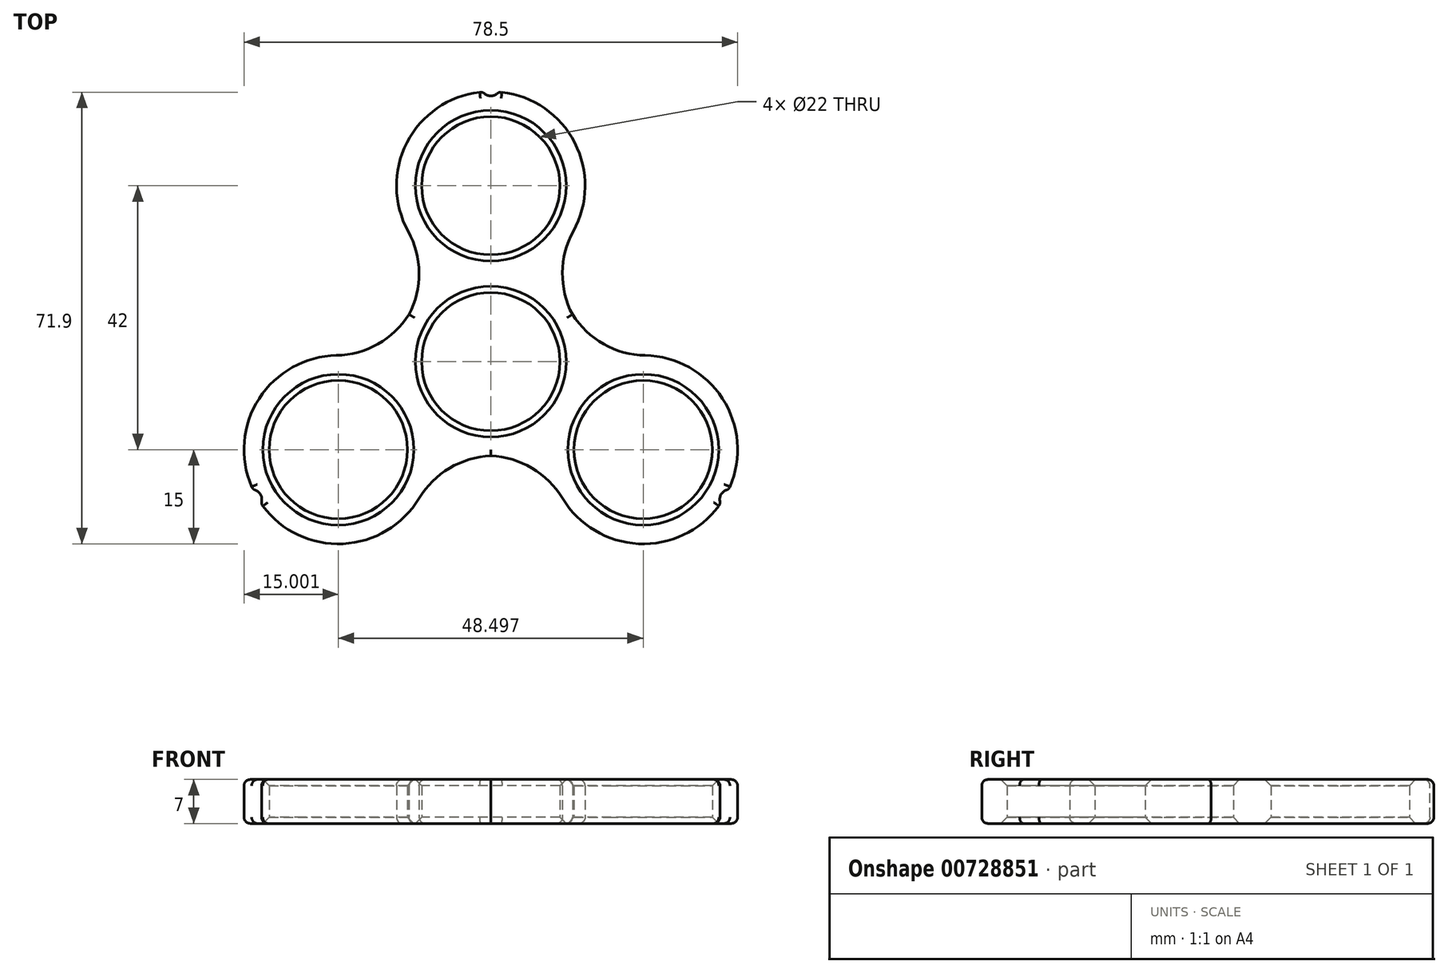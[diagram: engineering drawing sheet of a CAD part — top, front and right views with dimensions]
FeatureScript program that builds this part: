
annotation { "Feature Type Name" : "Feature", "Feature Type Description" : "" }
export const myFeature = defineFeature(function(context is Context, id is Id, definition is map)
    precondition{}
    {
        {
            var Q0;
            Q0=qCreatedBy(makeId("Top.planeOp"),FACE);
            var sketch = newSketch(context, id + "F0", { "sketchPlane" : qUnion([Q0])});
            skCircle(sketch, "E0", {"center": v(0, 0) * mm, "radius": 11 * mm});
            skCircle(sketch, "E1", {"center": v(0, 28) * mm, "radius": 11 * mm});
            skArc(sketch, "E2", {"start": v(12.67, 19.96) * mm, "mid": v(0, 43) * mm, "end": v(-12.67, 19.96) * mm});
            skArc(sketch, "E3", {"start": v(-12.67, 8.04) * mm, "mid": v(0, -15) * mm, "end": v(12.67, 8.04) * mm});
            skArc(sketch, "E4", {"start": v(13.14, 20.76) * mm, "mid": v(11.4, 14) * mm, "end": v(13.14, 7.24) * mm});
            skArc(sketch, "E5", {"start": v(-13.14, 7.24) * mm, "mid": v(-11.4, 14) * mm, "end": v(-13.14, 20.76) * mm});
            skSolve(sketch);
        }
        {
            var Q0;
            Q0=makeQuery(id+"F0.imprint","IMPRINT",FACE,{"disambiguationData":[TD([[makeQuery(id+"F0.imprint","IMPRINT",EDGE,{"derivedFrom":sQuery(id+"F0.wireOp",EDGE,"E0")}),-1.0]])]});
            extrude(context, id + "F1", {"entities" : qUnion([Q0]), "depth" : 7 * mm, "offsetDistance" : 25 * mm});
        }
        {
            var Q0;
            Q0=makeQuery(id+"F1.opExtrude","CAP_EDGE",EDGE,{"disambiguationData":[OSD([sQuery(id+"F0.wireOp",EDGE,"E2")])],"isStart":false});
            var Q1;
            Q1=makeQuery(id+"F1.opExtrude","CAP_EDGE",EDGE,{"disambiguationData":[OSD([sQuery(id+"F0.wireOp",EDGE,"E2")])],"isStart":true});
            fillet(context, id + "F2", {"entities" : qUnion([Q0, Q1]), "radius" : 1 * mm, "tangentPropagation" : true, "allowEdgeOverflow" : false});
        }
        {
            var Q0;
            Q0=qCreatedBy(makeId("Top.planeOp"),FACE);
            var sketch = newSketch(context, id + "F3", { "sketchPlane" : qUnion([Q0])});
            skCircle(sketch, "E6", {"center": v(0, 43.78) * mm, "radius": 1.5 * mm});
            skSolve(sketch);
        }
        {
            var Q0;
            Q0=makeQuery(id+"F3.imprint","IMPRINT",FACE,{"disambiguationData":[TD([[makeQuery(id+"F3.imprint","IMPRINT",EDGE,{"derivedFrom":sQuery(id+"F3.wireOp",EDGE,"E6")}),1.0]])]});
            extrude(context, id + "F4", {"entities" : qUnion([Q0]), "operationType" : NewBodyOperationType.REMOVE, "oppositeDirection" : true, "depth" : 25 * mm, "offsetDistance" : 25 * mm, "hasSecondDirection" : true, "secondDirectionOppositeDirection" : false, "secondDirectionDepth" : 25 * mm});
        }
        {
            var Q0;
            Q0=makeQuery(id+"F4.boolean.opBoolean","INTERSECT",EDGE,{"disambiguationData":[OD(1.0)],"derivedFrom":[makeQuery(id+"F1.opExtrude","SWEPT_FACE",FACE,{"disambiguationData":[OSD([sQuery(id+"F0.wireOp",EDGE,"E2")])]}),makeQuery(id+"F4.opExtrude","SWEPT_FACE",FACE,{"disambiguationData":[OSD([sQuery(id+"F3.wireOp",EDGE,"E6")])]})]});
            fillet(context, id + "F5", {"entities" : qUnion([Q0]), "radius" : 1 * mm, "tangentPropagation" : true, "allowEdgeOverflow" : false});
        }
        {
            var Q0;
            Q0=makeQuery(id+"F1.opExtrude","CAP_EDGE",EDGE,{"disambiguationData":[OSD([sQuery(id+"F0.wireOp",EDGE,"E1")])],"isStart":false});
            var Q1;
            Q1=makeQuery(id+"F1.opExtrude","CAP_EDGE",EDGE,{"disambiguationData":[OSD([sQuery(id+"F0.wireOp",EDGE,"E0")])],"isStart":false});
            var Q2;
            Q2=makeQuery(id+"F1.opExtrude","CAP_EDGE",EDGE,{"disambiguationData":[OSD([sQuery(id+"F0.wireOp",EDGE,"E0")])],"isStart":true});
            var Q3;
            Q3=makeQuery(id+"F1.opExtrude","CAP_EDGE",EDGE,{"disambiguationData":[OSD([sQuery(id+"F0.wireOp",EDGE,"E1")])],"isStart":true});
            chamfer(context, id + "F6", {"entities" : qUnion([Q0, Q1, Q2, Q3]), "width" : 1 * mm, "tangentPropagation" : true});
        }
        {
            var Q0;
            Q0=makeQuery(id+"F1.opExtrude","SWEPT_BODY",BODY,{"disambiguationData":[OSD([sQuery(id+"F0.wireOp",EDGE,"E0"),sQuery(id+"F0.wireOp",EDGE,"E1"),sQuery(id+"F0.wireOp",EDGE,"E2"),sQuery(id+"F0.wireOp",EDGE,"E3"),sQuery(id+"F0.wireOp",EDGE,"Ec2Vlz0A-VpfN-5pEN-I0C1-ma1xhHcSJPSF"),sQuery(id+"F0.wireOp",EDGE,"MxbFCYLW-GsdS-lCaN-WZZZ-vl0BdLRhMUwP")])]});
            var Q1;
            Q1=makeQuery(id+"F1.opExtrude","SWEPT_FACE",FACE,{"disambiguationData":[OSD([sQuery(id+"F0.wireOp",EDGE,"E0")])]});
            circularPattern(context, id + "F7", {"operationType" : NewBodyOperationType.ADD, "entities" : qUnion([Q0]), "axis" : qUnion([Q1]), "angle" : 360 * degree, "instanceCount" : 3, "equalSpace" : true});
        }
    });
